# Revit family: Hager-Volta-IP30-Hollow_wall-sistema-NoHosted-PT-pt
name_source: partatom
category: Electrical Equipment
units: mm (PartAtom-declared; Revit-internal decimal feet)

## family parameters
Always vertical = Yes
Cut with Voids When Loaded = No
Panel Configuration = Two Columns, Circuits Across
Part Type = Panelboard
Room Calculation Point = No
Round Connector Dimension = Use Diameter
Shared = No
Work Plane-Based = Yes

## types (1)
- Montagem embutida IP30 L348 A880.5 P94.5 12 unidade de divisão - VH60EP
    Default Elevation = 1219 mm
    EF000003 - Método de montagem = EV000128 - Parede oca
    EF000007 - Cor = EV000202 - Branco
    EF000008 - Largura = 348 mm  [stored 1.14173 ft]
    EF000040 - Altura = 880 mm  [stored 2.88714 ft]
    EF000049 - Profundidade = 94 mm  [stored 0.308399 ft]
    EF000116 - Número RAL = 9010
    EF000118 - Com tampa de montagem = No
    EF000218 - Profundidade incorporada = 90 mm  [stored 0.295276 ft]
    EF000266 - Número de linhas = 5
    EF000332 - Altura embutida = 846 mm  [stored 2.77559 ft]
    EF000339 - Tipo de difusor = EV004216 - Porta
    EF000846 - Largura para embutir = 314 mm  [stored 1.03018 ft]
    EF001062 - Versão EMC = No
    EF001088 - Extensão possível = Yes
    EF001131 - Profundidade interior = 92 mm
    EF001134 - Calha DIN = Yes
    EF001596 - Material do corpo = EV000154 - Outro
    EF002950 - Largura em número de módulos = 12
    EF004462 - Tipo de fecho = EV000154 - Outro
    EF005474 - Grau de proteção (IP) = EV006410 - IP30
    EF006244 - Tampa/porta transparente = No
    EF006306 - Com fecho = No
    EF009212 - Tipo de tampa = EV009916 - Com recuo
    EF015776 - Borne de terra = Yes
    EF015777 - Borne de neutro = No
    EF015941 - Porta para passagem de sinal = No
    HG000001 - Número de colunas = 1
    HG000002 - Com porta ou tampa = Yes
    HG000003 - Gama = Volta
    HG000004 - Referência do Fabricante = VH60EP
    HG000005 - Espessura = 3 mm  [stored 0.00984252 ft]
    HG000006 - Encastrado = Yes
    HG000007 - Número de colunas vazias = 0
    HG000008 - Número de filas vazias = 0
    HG000009 - Porta dupla = No
    HG000010 - Portas assimétricas = No
    HG000011 - Filas vazias desde da parte de baixo = No
    HG000017 - Distância entre polos = 18 mm  [stored 0.0590551 ft]
    Manufacturer = Hager
    Model = VH60EP
    Type Comments = Volta

note: [stored X ft] marks values corroborated as IEEE doubles in the binary element streams (Revit-internal decimal feet)

## geometry (parser evidence)
native form markers: Sweep x12
no freeform markers — native parametric forms only
